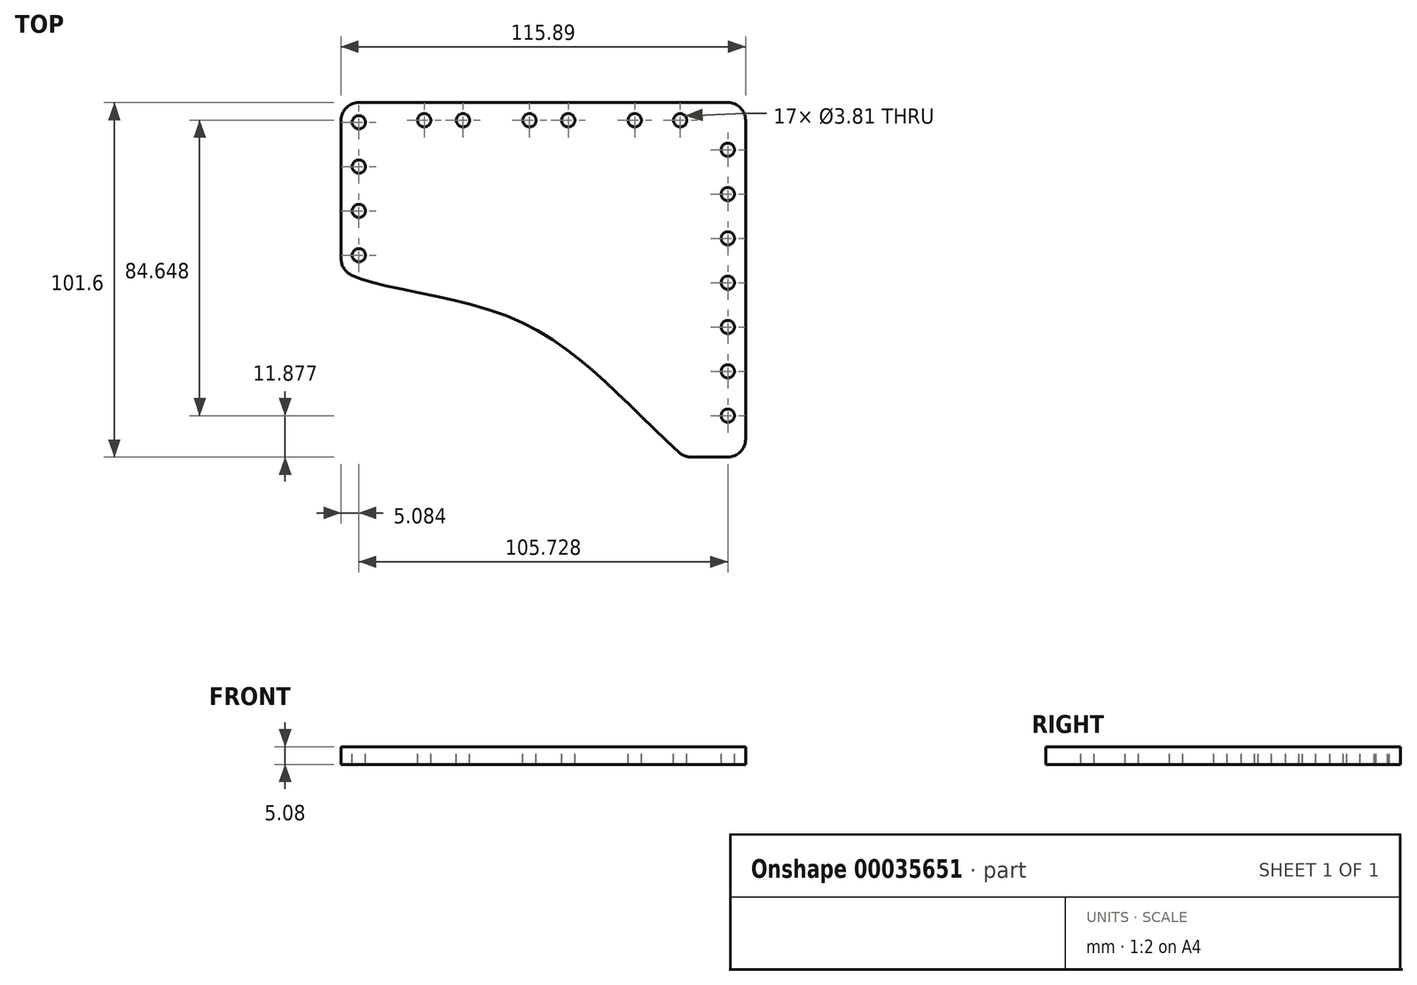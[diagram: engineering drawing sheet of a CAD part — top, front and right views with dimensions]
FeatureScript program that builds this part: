
annotation { "Feature Type Name" : "Feature", "Feature Type Description" : "" }
export const myFeature = defineFeature(function(context is Context, id is Id, definition is map)
    precondition{}
    {
        {
            var Q0;
            Q0=qCreatedBy(makeId("Top.planeOp"),FACE);
            var sketch = newSketch(context, id + "F0", { "sketchPlane" : qUnion([Q0])});
            skFitSpline(sketch, "E0", {"points": [v(-70.12, -7.3) * mm, v(-21.72, -21.55) * mm, v(28.18, -61.59) * mm], "startDerivative": vector(32.32, -38.35) * mm, "endDerivative": vector(93.32, -82.03) * mm});
            skLineSegment(sketch, "E1", {"start": v(28.18, -61.59) * mm, "end": v(45.77, -61.59) * mm});
            skLineSegment(sketch, "E2", {"start": v(45.77, -61.59) * mm, "end": v(45.77, 40.01) * mm});
            skLineSegment(sketch, "E3", {"start": v(45.77, 40.01) * mm, "end": v(-70.12, 40.01) * mm});
            skLineSegment(sketch, "E4", {"start": v(-70.12, 40.01) * mm, "end": v(-70.12, -7.3) * mm});
            skSolve(sketch);
        }
        {
            var Q0;
            Q0 = qSketchRegion(id + "F0", true);
            extrude(context, id + "F1", {"entities" : qUnion([Q0]), "depth" : 5.08 * mm});
        }
        {
            var Q0;
            Q0=makeQuery(id+"F1.opExtrude","SWEPT_EDGE",EDGE,{"disambiguationData":[OSD([sQuery(id+"F0.wireOp",EDGE,"E3"),sQuery(id+"F0.wireOp",EDGE,"E4")])]});
            var Q1;
            Q1=makeQuery(id+"F1.opExtrude","SWEPT_EDGE",EDGE,{"disambiguationData":[OSD([sQuery(id+"F0.wireOp",EDGE,"E2"),sQuery(id+"F0.wireOp",EDGE,"E3")])]});
            var Q2;
            Q2=makeQuery(id+"F1.opExtrude","SWEPT_EDGE",EDGE,{"disambiguationData":[OSD([sQuery(id+"F0.wireOp",EDGE,"E0"),sQuery(id+"F0.wireOp",EDGE,"E4")])]});
            var Q3;
            Q3=makeQuery(id+"F1.opExtrude","SWEPT_EDGE",EDGE,{"disambiguationData":[OSD([sQuery(id+"F0.wireOp",EDGE,"E0"),sQuery(id+"F0.wireOp",EDGE,"E1")])]});
            var Q4;
            Q4=makeQuery(id+"F1.opExtrude","SWEPT_EDGE",EDGE,{"disambiguationData":[OSD([sQuery(id+"F0.wireOp",EDGE,"E1"),sQuery(id+"F0.wireOp",EDGE,"E2")])]});
            fillet(context, id + "F2", {"entities" : qUnion([Q0, Q1, Q2, Q3, Q4]), "radius" : 5.08 * mm, "tangentPropagation" : true, "allowEdgeOverflow" : false});
        }
        {
            var Q0;
            Q0=makeQuery(id+"F1.opExtrude","CAP_FACE",FACE,{"disambiguationData":[OSD([sQuery(id+"F0.wireOp",EDGE,"E0"),sQuery(id+"F0.wireOp",EDGE,"E1"),sQuery(id+"F0.wireOp",EDGE,"E2"),sQuery(id+"F0.wireOp",EDGE,"E3"),sQuery(id+"F0.wireOp",EDGE,"E4")])],"isStart":false});
            var sketch = newSketch(context, id + "F3", { "sketchPlane" : qUnion([Q0])});
            skLineSegment(sketch, "E5", {"start": v(-65.04, 40.01) * mm, "end": v(-65.04, 0) * mm, "construction": true});
            skLineSegment(sketch, "E6", {"start": v(-70.12, 34.93) * mm, "end": v(45.77, 34.93) * mm, "construction": true});
            skCircle(sketch, "E7", {"center": v(-46.3, 34.93) * mm, "radius": 1.9 * mm});
            skCircle(sketch, "E8", {"center": v(-35.2, 34.93) * mm, "radius": 1.9 * mm});
            skCircle(sketch, "E9", {"center": v(-16.14, 34.93) * mm, "radius": 1.9 * mm});
            skCircle(sketch, "E10", {"center": v(-5.03, 34.93) * mm, "radius": 1.9 * mm});
            skCircle(sketch, "E11", {"center": v(14.02, 34.93) * mm, "radius": 1.9 * mm});
            skCircle(sketch, "E12", {"center": v(-65.04, 34.35) * mm, "radius": 1.9 * mm});
            skCircle(sketch, "E13", {"center": v(-65.04, 21.65) * mm, "radius": 1.9 * mm});
            skCircle(sketch, "E14", {"center": v(-65.04, 8.95) * mm, "radius": 1.9 * mm});
            skCircle(sketch, "E15", {"center": v(-65.04, -3.75) * mm, "radius": 1.9 * mm});
            skCircle(sketch, "E16", {"center": v(27.05, 34.93) * mm, "radius": 1.9 * mm});
            skLineSegment(sketch, "E17", {"start": v(40.7, 40.01) * mm, "end": v(40.7, -61.59) * mm, "construction": true});
            skCircle(sketch, "E18", {"center": v(40.7, 26.49) * mm, "radius": 1.9 * mm});
            skCircle(sketch, "E19", {"center": v(40.7, 13.79) * mm, "radius": 1.9 * mm});
            skCircle(sketch, "E20", {"center": v(40.7, 1.09) * mm, "radius": 1.9 * mm});
            skCircle(sketch, "E21", {"center": v(40.7, -11.61) * mm, "radius": 1.9 * mm});
            skCircle(sketch, "E22", {"center": v(40.7, -24.31) * mm, "radius": 1.9 * mm});
            skCircle(sketch, "E23", {"center": v(40.7, -37.01) * mm, "radius": 1.9 * mm});
            skCircle(sketch, "E24", {"center": v(40.7, -49.71) * mm, "radius": 1.9 * mm});
            skSolve(sketch);
        }
        {
            var Q0;
            Q0 = qSketchRegion(id + "F3", true);
            extrude(context, id + "F4", {"entities" : qUnion([Q0]), "operationType" : NewBodyOperationType.REMOVE, "endBound" : BoundingType.THROUGH_ALL, "oppositeDirection" : true, "depth" : 25.4 * mm});
        }
    });
